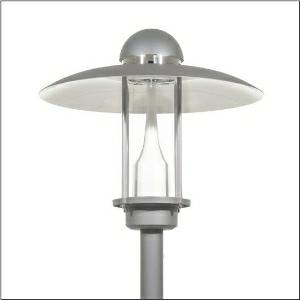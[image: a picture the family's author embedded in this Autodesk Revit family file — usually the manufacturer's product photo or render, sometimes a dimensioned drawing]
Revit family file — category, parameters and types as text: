
# Revit family: city-light_elegance_iq___st1_2a_5xa5265ef14h_e69b
name_source: partatom
category: Lighting Fixtures
units: mm (PartAtom-declared; Revit-internal decimal feet)

## family parameters
Cut with Voids When Loaded = No
Host = Face
Light Source = No
Part Type = Normal
Room Calculation Point = No
Round Connector Dimension = Use Diameter
Shared = No

## types (1)
- --- (1 x LED, 1470 lm, 10.5 W, 3000K)
    Apparent Load = 11 VA
    CIE Flux Codes = 22 62 94 98 100
    Color Rendering = 70
    Color Temperature = 3000K
    Default Elevation = 1800 mm
    Description = City-Light Elegance, mast luminaire, Module 540 iQ-SR, primary light control with 3 zone facetted reflector, of plastic, silver coated, highly specular, structured, primary optical cover: cover, of PMMA, transparent, light distribution: ST1.2a, light emission: direct distribution, primary light characteristic: asymmetric, installation type: post-top, LED, High Power LED, rated luminous flux: 1.470lm, luminous efficacy: 140lm/W, light colour: 730, colour temperature: 3000K, control gear: ECG iQ, control: Auto-Match, Temp-Guard, Lumen-Switch, Night-Set, Smart-Wire, Light-Fading, Desk-Remote (wireless, voltage-free reading and setting of iQ features in the workshop via application-optimized NFC function/RFID function), optimised constant luminous flux control (CLO 2.0), Street-Remote, presetting dimming logarithmic, with terminal, 6-pole, max. 2.5mm², mains connection: 220..240V, AC, 50/60Hz, start of lifetime: 11W, end of lifetime: 11W, reduction: 5W, luminaire housing, upper part, of aluminium, coated, Siteco® metallic grey (DB 702S), diameter: 750mm, height: 675mm, spigot size: d x l = 76 x 70mm (post-top) | with reducer (optional accessory) 60 x 70mm, post-top mast mounting element, of diecast aluminium, coated, Siteco® metallic grey (DB 702S), Module 540 iQ-SR, traffic white (RAL 9016), equipment: standard, protection rating (complete): IP65, insulation class (complete): insulation class II (safety insulation), certification: CE, ENEC, VDE, packaging unit: 1 piece

Light Distribution: ST1.2a
    Height = 675 mm
    Lamp = 1 x LED
    Lamp Light Flux = 1470 lm
    Lamp Power = 10.5 W
    Lamp count = 1
    Length = 750 mm
    Luminous efficacy = 140 lm/W
    Manufacturer = Siteco
    ModVariant = No
    Model = 5XA5265EF14H
    Number of Poles = 1
    OnlyDefault = Yes
    Power Factor = 1
    Product Name = City-Light Elegance iQ | ST1.2a
    Product group = mast luminaire | pylon top
    ProductGroupID = 6100
    Protection Class = Protection class II
    Protection Degree = IP 65
    RLX_Detail_Level = 1
    RlxData = <blob elided: 99453 chars, md5=5c93e5e6>
    Socket = socket
    Standby Power = 0 W
    System Light Flux = 1470 lm
    System Power = 11 W
    Type Comments = factory setting: luminous flux: 100 % | dim-lin: 254 | 419 mA
    Type Image = l_1006912.jpg
    URL = http://relux.com
    VarID = @adj_071101
    Voltage = 0 V
    Weight = 0.00 kg
    Width = 0 mm  [stored 0 ft]

note: [stored X ft] marks values corroborated as IEEE doubles in the binary element streams (Revit-internal decimal feet)

## geometry (parser evidence)
native form markers: Blend x4, Sweep x10
no freeform markers — native parametric forms only
